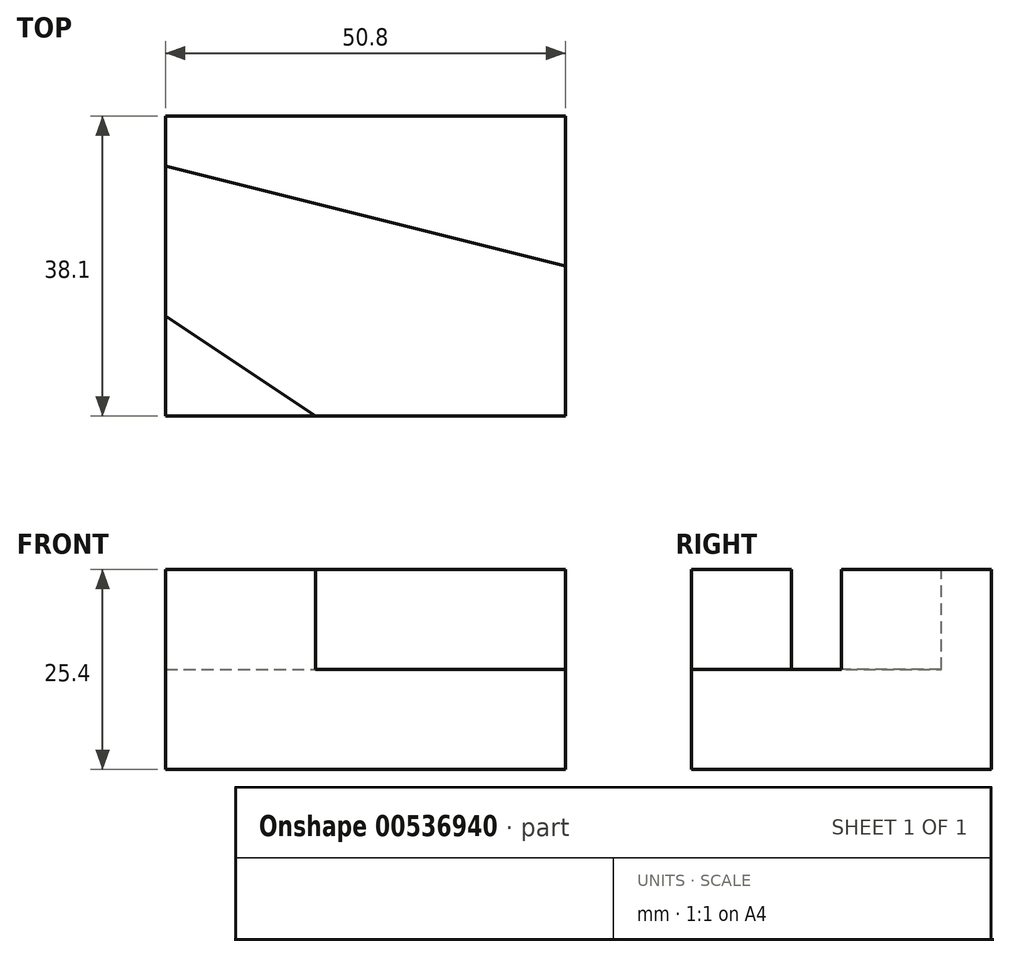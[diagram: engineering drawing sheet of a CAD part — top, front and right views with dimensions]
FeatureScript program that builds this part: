
annotation { "Feature Type Name" : "Feature", "Feature Type Description" : "" }
export const myFeature = defineFeature(function(context is Context, id is Id, definition is map)
    precondition{}
    {
        {
            var Q0;
            Q0=qCreatedBy(makeId("Front.planeOp"),FACE);
            var sketch = newSketch(context, id + "F0", { "sketchPlane" : qUnion([Q0])});
            skLineSegment(sketch, "E0.bottom", {"start": v(-24.61, 0) * mm, "end": v(26.19, 0) * mm});
            skLineSegment(sketch, "E0.top", {"start": v(-24.61, 25.4) * mm, "end": v(26.19, 25.4) * mm});
            skLineSegment(sketch, "E0.left", {"start": v(-24.61, 0) * mm, "end": v(-24.61, 25.4) * mm});
            skLineSegment(sketch, "E0.right", {"start": v(26.19, 0) * mm, "end": v(26.19, 25.4) * mm});
            skSolve(sketch);
        }
        {
            var Q0;
            Q0=makeQuery(id+"F0.imprint","IMPRINT",FACE,{"disambiguationData":[TD([[makeQuery(id+"F0.imprint","IMPRINT",EDGE,{"derivedFrom":sQuery(id+"F0.wireOp",EDGE,"E0.bottom")}),1.0]])]});
            extrude(context, id + "F1", {"entities" : qUnion([Q0]), "depth" : 38.1 * mm, "offsetDistance" : 25.4 * mm});
        }
        {
            var Q0;
            Q0=makeQuery(id+"F1.opExtrude","SWEPT_FACE",FACE,{"disambiguationData":[OSD([sQuery(id+"F0.wireOp",EDGE,"E0.top")])]});
            var sketch = newSketch(context, id + "F2", { "sketchPlane" : qUnion([Q0])});
            skLineSegment(sketch, "E1", {"start": v(-24.61, -6.35) * mm, "end": v(26.19, -19.05) * mm});
            skLineSegment(sketch, "E2", {"start": v(26.19, -19.05) * mm, "end": v(26.19, -38.1) * mm});
            skLineSegment(sketch, "E3", {"start": v(-5.56, -38.1) * mm, "end": v(-24.61, -25.4) * mm});
            skLineSegment(sketch, "E4", {"start": v(26.19, -38.1) * mm, "end": v(-5.56, -38.1) * mm});
            skLineSegment(sketch, "E5", {"start": v(-24.61, -25.4) * mm, "end": v(-24.61, -38.1) * mm});
            skLineSegment(sketch, "E6", {"start": v(-24.61, -38.1) * mm, "end": v(-5.56, -38.1) * mm});
            skSolve(sketch);
        }
        {
            var Q0;
            {var subQ1=sQuery(id+"F2.wireOp",EDGE,"E1");Q0=makeQuery(id+"F2.imprint","IMPRINT",FACE,{"disambiguationData":[TD([[makeQuery(id+"F2.imprint","IMPRINT",EDGE,{"derivedFrom":subQ1}),-1.0]])]});}
            extrude(context, id + "F3", {"entities" : qUnion([Q0]), "operationType" : NewBodyOperationType.REMOVE, "oppositeDirection" : true, "depth" : 12.7 * mm, "offsetDistance" : 25.4 * mm});
        }
    });
